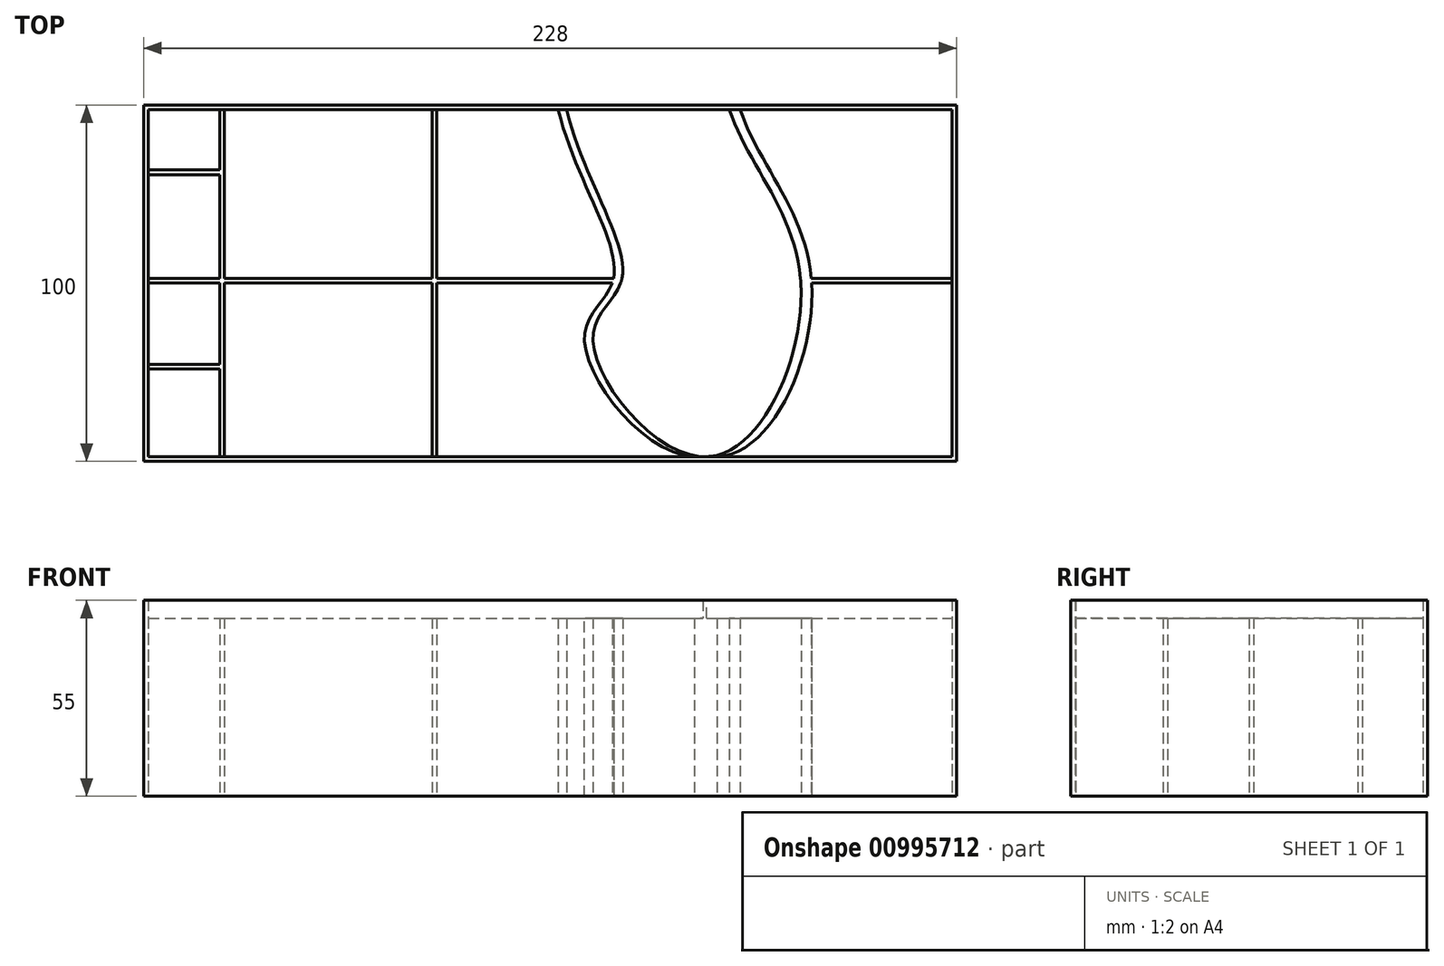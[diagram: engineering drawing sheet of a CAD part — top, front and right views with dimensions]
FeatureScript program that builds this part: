
annotation { "Feature Type Name" : "Feature", "Feature Type Description" : "" }
export const myFeature = defineFeature(function(context is Context, id is Id, definition is map)
    precondition{}
    {
        {
            var Q0;
            Q0=qCreatedBy(makeId("Top.planeOp"),FACE);
            var sketch = newSketch(context, id + "F0", { "sketchPlane" : qUnion([Q0])});
            skLineSegment(sketch, "E0.bottom", {"start": v(-180.4, 65.66) * mm, "end": v(47.6, 65.66) * mm});
            skLineSegment(sketch, "E0.top", {"start": v(-180.4, -34.34) * mm, "end": v(47.6, -34.34) * mm});
            skLineSegment(sketch, "E0.left", {"start": v(-180.4, 65.66) * mm, "end": v(-180.4, -34.34) * mm});
            skLineSegment(sketch, "E0.right", {"start": v(47.6, 65.66) * mm, "end": v(47.6, -34.34) * mm});
            skLineSegment(sketch, "E1.0", {"start": v(46.3, 64.36) * mm, "end": v(46.3, 16.96) * mm});
            skLineSegment(sketch, "E1.1", {"start": v(-179.1, 64.36) * mm, "end": v(-159.1, 64.36) * mm});
            skLineSegment(sketch, "E1.2", {"start": v(-179.1, 64.36) * mm, "end": v(-179.1, 47.43) * mm});
            skLineSegment(sketch, "E1.3", {"start": v(-179.1, -33.04) * mm, "end": v(-159.1, -33.04) * mm});
            skLineSegment(sketch, "E2.left", {"start": v(-159.1, -33.04) * mm, "end": v(-159.1, -8.46) * mm});
            skLineSegment(sketch, "E2.right", {"start": v(-157.8, -33.04) * mm, "end": v(-157.8, 15.66) * mm});
            skLineSegment(sketch, "E3.bottom", {"start": v(-179.1, 46.13) * mm, "end": v(-159.1, 46.13) * mm});
            skLineSegment(sketch, "E3.top", {"start": v(-179.1, 47.43) * mm, "end": v(-159.1, 47.43) * mm});
            skLineSegment(sketch, "E4.bottom", {"start": v(-179.1, -8.46) * mm, "end": v(-159.1, -8.46) * mm});
            skLineSegment(sketch, "E4.top", {"start": v(-179.1, -7.16) * mm, "end": v(-159.1, -7.16) * mm});
            skLineSegment(sketch, "E5.bottom", {"start": v(-179.1, 15.66) * mm, "end": v(-159.1, 15.66) * mm});
            skLineSegment(sketch, "E5.top", {"start": v(-179.1, 16.96) * mm, "end": v(-159.1, 16.96) * mm});
            skPoint(sketch, "E6.oppositeSnap0", {"position": v(-157.8, 15.66) * mm});
            skLineSegment(sketch, "E6.bottom", {"start": v(-157.8, 16.96) * mm, "end": v(-99.5, 16.96) * mm});
            skLineSegment(sketch, "E6.top", {"start": v(-157.8, 15.66) * mm, "end": v(-99.5, 15.66) * mm});
            skLineSegment(sketch, "E7.left", {"start": v(-99.5, -33.04) * mm, "end": v(-99.5, 15.66) * mm});
            skLineSegment(sketch, "E7.right", {"start": v(-98.2, -33.04) * mm, "end": v(-98.2, 15.66) * mm});
            skLineSegment(sketch, "E8", {"start": v(-99.5, 16.96) * mm, "end": v(-99.5, 64.36) * mm});
            skFitSpline(sketch, "E9", {"points": [v(-61.78, 64.36) * mm, v(-46.28, 16.96) * mm, v(-54.46, 0) * mm, v(-22.6, -33.04) * mm, v(3.89, 15.66) * mm, v(-16.14, 64.36) * mm], "startDerivative": vector(64.61, -272.48) * mm, "endDerivative": vector(-68.57, 211.5) * mm});
            skFitSpline(sketch, "E10", {"points": [v(-64.13, 64.36) * mm, v(-48.63, 16.96) * mm, v(-56.8, 0) * mm, v(-24.94, -33.04) * mm, v(1.54, 15.66) * mm, v(-18.48, 64.36) * mm], "startDerivative": vector(64.61, -272.48) * mm, "endDerivative": vector(-68.57, 211.5) * mm});
            skFitSpline(sketch, "E11", {"points": [v(-58.76, 64.36) * mm, v(-43.25, 16.96) * mm, v(-51.44, 0) * mm, v(-19.57, -33.04) * mm, v(6.91, 15.66) * mm, v(-13.11, 64.36) * mm], "startDerivative": vector(64.61, -272.48) * mm, "endDerivative": vector(-68.57, 211.5) * mm});
            skLineSegment(sketch, "E12", {"start": v(-98.2, 16.96) * mm, "end": v(-98.2, 64.36) * mm});
            skLineSegment(sketch, "E13.trimOffspring", {"start": v(-46.28, 16.96) * mm, "end": v(3.79, 16.96) * mm});
            skLineSegment(sketch, "E14.trimOffspring", {"start": v(-46.64, 15.66) * mm, "end": v(3.89, 15.66) * mm});
            skLineSegment(sketch, "E15.trimOffspring", {"start": v(6.82, 16.96) * mm, "end": v(46.3, 16.96) * mm});
            skLineSegment(sketch, "E16.trimOffspring", {"start": v(6.91, 15.66) * mm, "end": v(46.3, 15.66) * mm});
            skLineSegment(sketch, "E17.trimOffspring", {"start": v(-98.2, 16.96) * mm, "end": v(-48.63, 16.96) * mm});
            skLineSegment(sketch, "E18.trimOffspring", {"start": v(-98.2, 15.66) * mm, "end": v(-49, 15.66) * mm});
            skLineSegment(sketch, "E19.trimOffspring", {"start": v(-61.78, 64.36) * mm, "end": v(-16.14, 64.36) * mm});
            skLineSegment(sketch, "E20.trimOffspring", {"start": v(-13.11, 64.36) * mm, "end": v(46.3, 64.36) * mm});
            skLineSegment(sketch, "E21.trimOffspring", {"start": v(46.3, 15.66) * mm, "end": v(46.3, -33.04) * mm});
            skPoint(sketch, "E22.start.orphan", {"position": v(47.6, 0) * mm});
            skLineSegment(sketch, "E23.trimOffspring", {"start": v(-24.94, -33.04) * mm, "end": v(-24.94, -33.04) * mm});
            skLineSegment(sketch, "E24.trimOffspring", {"start": v(-19.57, -33.04) * mm, "end": v(46.3, -33.04) * mm});
            skLineSegment(sketch, "E25.trimOffspring", {"start": v(-23.62, -33.04) * mm, "end": v(-22.6, -33.04) * mm});
            skLineSegment(sketch, "E26.trimOffspring", {"start": v(-98.2, -33.04) * mm, "end": v(-25.96, -33.04) * mm});
            skLineSegment(sketch, "E27.trimOffspring", {"start": v(-98.2, 64.36) * mm, "end": v(-64.13, 64.36) * mm});
            skLineSegment(sketch, "E28.trimOffspring", {"start": v(-157.8, 64.36) * mm, "end": v(-99.5, 64.36) * mm});
            skLineSegment(sketch, "E29.trimOffspring", {"start": v(-159.1, 47.43) * mm, "end": v(-159.1, 64.36) * mm});
            skLineSegment(sketch, "E30.trimOffspring", {"start": v(-179.1, 46.13) * mm, "end": v(-179.1, 16.96) * mm});
            skLineSegment(sketch, "E31.trimOffspring", {"start": v(-157.8, 16.96) * mm, "end": v(-157.8, 64.36) * mm});
            skLineSegment(sketch, "E32.trimOffspring", {"start": v(-159.1, 16.96) * mm, "end": v(-159.1, 46.13) * mm});
            skLineSegment(sketch, "E33.trimOffspring", {"start": v(-179.1, 15.66) * mm, "end": v(-179.1, -7.16) * mm});
            skLineSegment(sketch, "E34.trimOffspring", {"start": v(-179.1, -8.46) * mm, "end": v(-179.1, -33.04) * mm});
            skLineSegment(sketch, "E35.trimOffspring", {"start": v(-159.1, -7.16) * mm, "end": v(-159.1, 15.66) * mm});
            skLineSegment(sketch, "E36.trimOffspring", {"start": v(-157.8, -33.04) * mm, "end": v(-99.5, -33.04) * mm});
            skSolve(sketch);
        }
        {
            var Q0;
            Q0=makeQuery(id+"F0.imprint","IMPRINT",FACE,{"disambiguationData":[TD([[makeQuery(id+"F0.imprint","IMPRINT",EDGE,{"derivedFrom":sQuery(id+"F0.wireOp",EDGE,"E0.bottom")}),-1.0]])]});
            extrude(context, id + "F1", {"entities" : qUnion([Q0]), "depth" : 55 * mm, "offsetDistance" : 25 * mm});
        }
        {
            var Q0;
            Q0=makeQuery(id+"F1.opExtrude","CAP_FACE",FACE,{"disambiguationData":[OSD([sQuery(id+"F0.wireOp",EDGE,"E0.bottom"),sQuery(id+"F0.wireOp",EDGE,"E0.top"),sQuery(id+"F0.wireOp",EDGE,"E0.left"),sQuery(id+"F0.wireOp",EDGE,"E0.right"),sQuery(id+"F0.wireOp",EDGE,"E1.0"),sQuery(id+"F0.wireOp",EDGE,"E1.1"),sQuery(id+"F0.wireOp",EDGE,"E1.2"),sQuery(id+"F0.wireOp",EDGE,"E1.3"),sQuery(id+"F0.wireOp",EDGE,"E2.left"),sQuery(id+"F0.wireOp",EDGE,"E2.right"),sQuery(id+"F0.wireOp",EDGE,"E3.bottom"),sQuery(id+"F0.wireOp",EDGE,"E3.top"),sQuery(id+"F0.wireOp",EDGE,"E4.bottom"),sQuery(id+"F0.wireOp",EDGE,"E4.top"),sQuery(id+"F0.wireOp",EDGE,"E5.bottom"),sQuery(id+"F0.wireOp",EDGE,"E5.top"),sQuery(id+"F0.wireOp",EDGE,"E6.bottom"),sQuery(id+"F0.wireOp",EDGE,"E6.top"),sQuery(id+"F0.wireOp",EDGE,"E7.left"),sQuery(id+"F0.wireOp",EDGE,"E7.right"),sQuery(id+"F0.wireOp",EDGE,"E8"),sQuery(id+"F0.wireOp",EDGE,"E9"),sQuery(id+"F0.wireOp",EDGE,"E9"),sQuery(id+"F0.wireOp",EDGE,"E10"),sQuery(id+"F0.wireOp",EDGE,"E11"),sQuery(id+"F0.wireOp",EDGE,"E12"),sQuery(id+"F0.wireOp",EDGE,"E13.trimOffspring"),sQuery(id+"F0.wireOp",EDGE,"E10"),sQuery(id+"F0.wireOp",EDGE,"E9"),sQuery(id+"F0.wireOp",EDGE,"E14.trimOffspring"),sQuery(id+"F0.wireOp",EDGE,"E9"),sQuery(id+"F0.wireOp",EDGE,"E11"),sQuery(id+"F0.wireOp",EDGE,"E15.trimOffspring"),sQuery(id+"F0.wireOp",EDGE,"E16.trimOffspring"),sQuery(id+"F0.wireOp",EDGE,"E17.trimOffspring"),sQuery(id+"F0.wireOp",EDGE,"E18.trimOffspring"),sQuery(id+"F0.wireOp",EDGE,"E19.trimOffspring"),sQuery(id+"F0.wireOp",EDGE,"E20.trimOffspring"),sQuery(id+"F0.wireOp",EDGE,"E21.trimOffspring"),sQuery(id+"F0.wireOp",EDGE,"E24.trimOffspring"),sQuery(id+"F0.wireOp",EDGE,"E26.trimOffspring"),sQuery(id+"F0.wireOp",EDGE,"E27.trimOffspring"),sQuery(id+"F0.wireOp",EDGE,"E28.trimOffspring"),sQuery(id+"F0.wireOp",EDGE,"E29.trimOffspring"),sQuery(id+"F0.wireOp",EDGE,"E30.trimOffspring"),sQuery(id+"F0.wireOp",EDGE,"E31.trimOffspring"),sQuery(id+"F0.wireOp",EDGE,"E32.trimOffspring"),sQuery(id+"F0.wireOp",EDGE,"E33.trimOffspring"),sQuery(id+"F0.wireOp",EDGE,"E34.trimOffspring"),sQuery(id+"F0.wireOp",EDGE,"E35.trimOffspring"),sQuery(id+"F0.wireOp",EDGE,"E36.trimOffspring")])],"isStart":false});
            var sketch = newSketch(context, id + "F2", { "sketchPlane" : qUnion([Q0])});
            skLineSegment(sketch, "E37.bottom", {"start": v(-179.1, -33.04) * mm, "end": v(46.3, -33.04) * mm});
            skLineSegment(sketch, "E37.top", {"start": v(-179.1, 64.36) * mm, "end": v(46.3, 64.36) * mm});
            skLineSegment(sketch, "E37.left", {"start": v(-179.1, -33.04) * mm, "end": v(-179.1, 64.36) * mm});
            skLineSegment(sketch, "E37.right", {"start": v(46.3, -33.04) * mm, "end": v(46.3, 64.36) * mm});
            skSolve(sketch);
        }
        {
            var Q0;
            Q0 = qSketchRegion(id + "F2", true);
            extrude(context, id + "F3", {"entities" : qUnion([Q0]), "operationType" : NewBodyOperationType.REMOVE, "oppositeDirection" : true, "depth" : 5 * mm, "offsetDistance" : 25 * mm});
        }
    });
